# Revit family: Louver-Penthouse-Carnes-Post_Corner-PDBB
name_source: partatom
category: Air Terminals
revit_build: Autodesk Revit Architecture 2012 (Build: 20110916_2132(x64)
units: mm (PartAtom-declared; Revit-internal decimal feet)

## types (1)
- (See Type Catalog)
    04 CSI = 08 91 00
    1 In 12 Pitched Roof = No
    3 in 12 Pitched Roof = Yes
    95 CSI = 10200
    Assembly Code = D3090700
    Blade Material = Aluminum - Carnes - Extruded
    Blades Length = 51"
    Blades Quantity = 8
    Blades Quantity Control = 7
    Blades Width = 51"
    Catalog URL = http://www.carnes.com
    Connector Description 1 = Duct Connection 1
    Corners Covers Height = 20 5/32"
    Custom Length = 220"
    Description = Drainable Blade Penthouses
    Flat Roof = No
    Frame Material = Aluminum - Carnes - Extruded
    Free Area = 0 SF
    Free Area Note = See Spec Sheet URL
    Height Note = User should verify available heights in Spec Sheet URL
    Length Control = 48"
    Louver Height = 24"
    Louver Length = 48"
    Louver Width = 48"
    Manufacturer = Carnes Company
    Manufacturer Fax = 608-845-6470
    Maximum Size Note = 72"W x 220"L x 80"H, unlimited size with multiple section assembly.
    Meets Building Code Standards = See Catalog URL
    Minimum Size = 12"W x 12"L x 10.5"H
    Model = PDBB
    Multiple Blades Visibility = Yes
    Pitched Roof Visibility = Yes
    Point of Water Penetration = 1250 FPM
    Pressure Drop = 0.00 Pa
    Product Line = Drainable Blade Penthouses
    Product Page URL = http://www.carnes.com
    Rectangular Length = No
    Roof Pitch = 14.04°
    Single Blade Visibility = No
    Specifications  URL = http://www.carnes.com
    Subcategory = Louvers and Dampers
    URL = http://www.carnes.com
    ecoScorecard Product Page = http://ecoscorecard.com

## geometry (parser evidence)
native form markers: Blend x4, Sweep x4
no freeform markers — native parametric forms only
